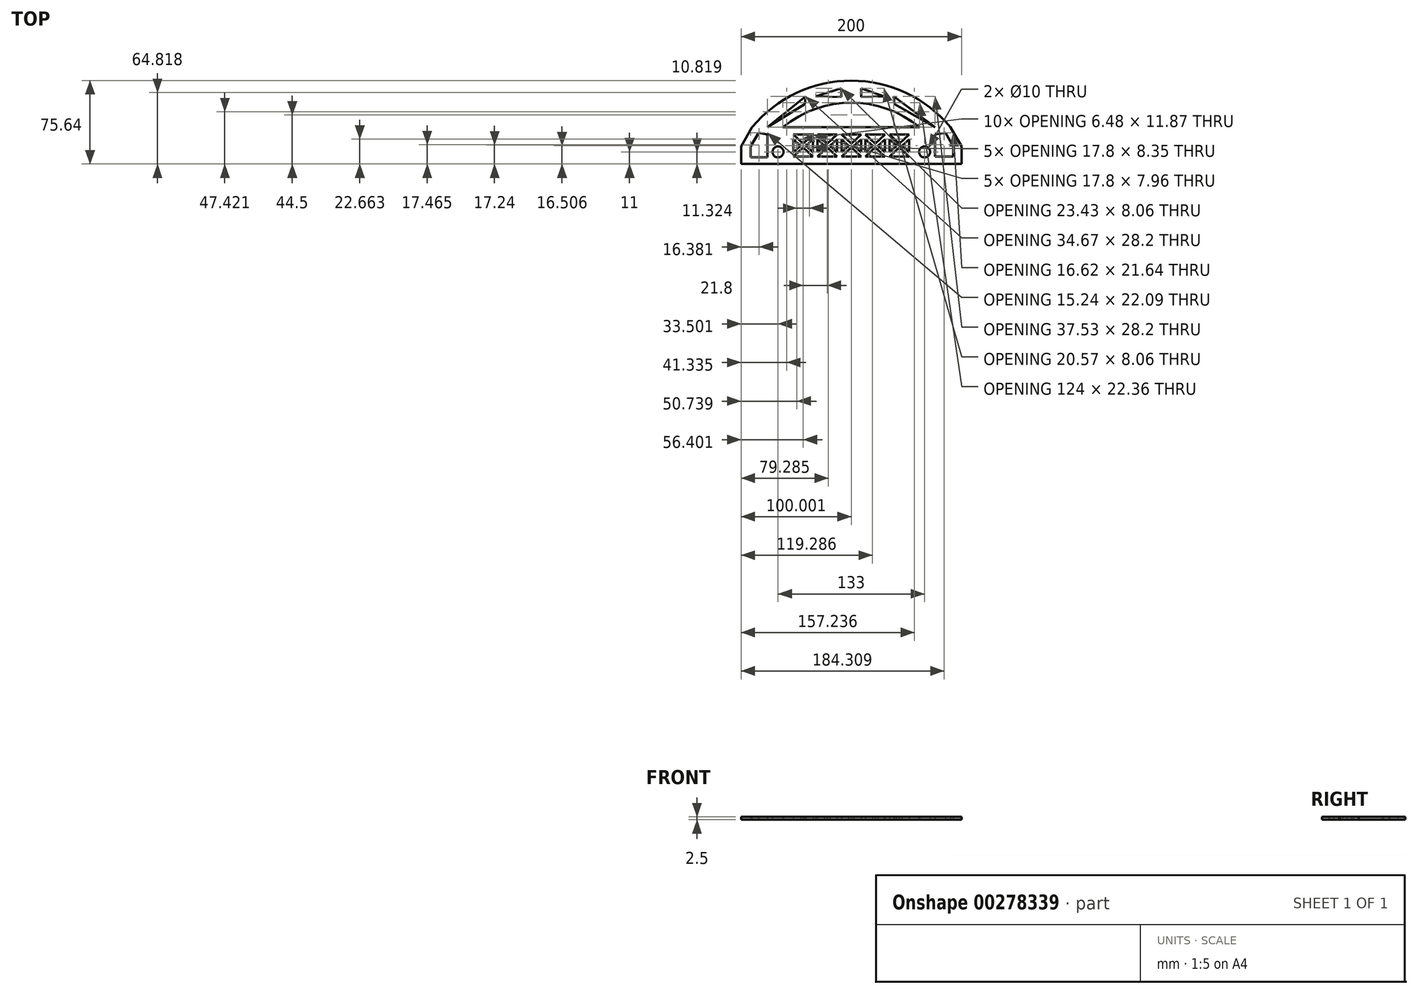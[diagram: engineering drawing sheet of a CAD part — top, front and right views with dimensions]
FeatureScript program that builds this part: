
annotation { "Feature Type Name" : "Feature", "Feature Type Description" : "" }
export const myFeature = defineFeature(function(context is Context, id is Id, definition is map)
    precondition{}
    {
        {
            var Q0;
            Q0=qCreatedBy(makeId("Top.planeOp"),FACE);
            var sketch = newSketch(context, id + "F0", { "sketchPlane" : qUnion([Q0])});
            skLineSegment(sketch, "E0.top", {"start": v(-97.14, -33.32) * mm, "end": v(102.86, -33.32) * mm});
            skLineSegment(sketch, "E0.left", {"start": v(-97.14, -17.32) * mm, "end": v(-97.14, -33.32) * mm});
            skLineSegment(sketch, "E0.right", {"start": v(102.86, -17.32) * mm, "end": v(102.86, -33.32) * mm});
            skCircle(sketch, "E1", {"center": v(-63.64, -22.32) * mm, "radius": 5 * mm});
            skCircle(sketch, "E2", {"center": v(69.36, -22.32) * mm, "radius": 5 * mm});
            skPoint(sketch, "E3", {"position": v(-63.64, -33.32) * mm});
            skPoint(sketch, "E4", {"position": v(69.36, -33.32) * mm});
            skLineSegment(sketch, "E5", {"start": v(-63.64, -33.32) * mm, "end": v(-97.14, -33.32) * mm});
            skLineSegment(sketch, "E6", {"start": v(69.36, -33.32) * mm, "end": v(102.86, -33.32) * mm});
            skLineSegment(sketch, "E7", {"start": v(-97.14, -17.32) * mm, "end": v(-87.14, 0) * mm});
            skLineSegment(sketch, "E8", {"start": v(102.86, -17.32) * mm, "end": v(92.86, 0) * mm});
            skArc(sketch, "E9", {"start": v(92.86, 0) * mm, "mid": v(2.86, 42.32) * mm, "end": v(-87.14, 0) * mm});
            skPoint(sketch, "E10", {"position": v(-59.14, 0) * mm});
            skPoint(sketch, "E11", {"position": v(64.86, 0) * mm});
            skArc(sketch, "E12", {"start": v(64.86, 0) * mm, "mid": v(2.86, 22.36) * mm, "end": v(-59.14, 0) * mm});
            skLineSegment(sketch, "E13", {"start": v(-59.14, 0) * mm, "end": v(64.86, 0) * mm});
            skLineSegment(sketch, "E14", {"start": v(0, 0) * mm, "end": v(-59.14, 0) * mm});
            skPoint(sketch, "E15", {"position": v(-29.57, 28.2) * mm});
            skPoint(sketch, "E15.positionSnap0", {"position": v(-29.57, 0) * mm});
            skLineSegment(sketch, "E16", {"start": v(0, 0) * mm, "end": v(64.86, 0) * mm});
            skPoint(sketch, "E17", {"position": v(32.43, 28.2) * mm});
            skPoint(sketch, "E17.positionSnap0", {"position": v(32.43, 0) * mm});
            skPoint(sketch, "E18", {"position": v(2.86, -33.32) * mm});
            skPoint(sketch, "E19", {"position": v(2.86, 32.96) * mm});
            skLineSegment(sketch, "E20", {"start": v(11.86, 35.53) * mm, "end": v(11.86, 27.47) * mm});
            skLineSegment(sketch, "E21", {"start": v(-6.14, 35.53) * mm, "end": v(-6.14, 27.47) * mm});
            skLineSegment(sketch, "E22", {"start": v(11.86, 35.53) * mm, "end": v(32.43, 28.2) * mm});
            skLineSegment(sketch, "E23", {"start": v(11.86, 27.47) * mm, "end": v(32.43, 28.2) * mm});
            skLineSegment(sketch, "E24", {"start": v(-6.14, 35.53) * mm, "end": v(-29.57, 28.2) * mm});
            skLineSegment(sketch, "E25", {"start": v(-6.14, 27.47) * mm, "end": v(-29.57, 28.2) * mm});
            skPoint(sketch, "E26", {"position": v(-73.14, 0) * mm});
            skLineSegment(sketch, "E27", {"start": v(-39.14, 21.24) * mm, "end": v(-73.14, 0) * mm});
            skPoint(sketch, "E28", {"position": v(78.86, 0) * mm});
            skPoint(sketch, "E29", {"position": v(42, 21.24) * mm});
            skLineSegment(sketch, "E30", {"start": v(42, 21.24) * mm, "end": v(78.86, 0) * mm});
            skPoint(sketch, "E31", {"position": v(-38.47, 28.2) * mm});
            skLineSegment(sketch, "E32", {"start": v(-38.47, 28.2) * mm, "end": v(-73.14, 0) * mm});
            skLineSegment(sketch, "E33", {"start": v(-38.47, 28.2) * mm, "end": v(-39.14, 21.24) * mm});
            skPoint(sketch, "E34", {"position": v(41.33, 28.2) * mm});
            skLineSegment(sketch, "E35", {"start": v(41.33, 28.2) * mm, "end": v(42, 21.24) * mm});
            skLineSegment(sketch, "E36", {"start": v(41.33, 28.2) * mm, "end": v(78.86, 0) * mm});
            skPoint(sketch, "E37", {"position": v(-49.64, -6.67) * mm});
            skPoint(sketch, "E38", {"position": v(-31.84, -6.67) * mm});
            skLineSegment(sketch, "E39", {"start": v(-49.64, -6.67) * mm, "end": v(-31.84, -6.67) * mm});
            skPoint(sketch, "E40", {"position": v(-40.74, -14.64) * mm});
            skPoint(sketch, "E40.positionSnap0", {"position": v(-40.74, -6.67) * mm});
            skPoint(sketch, "E41", {"position": v(-40.74, -18.33) * mm});
            skPoint(sketch, "E42", {"position": v(-49.64, -26.67) * mm});
            skPoint(sketch, "E43", {"position": v(-31.84, -26.67) * mm});
            skLineSegment(sketch, "E44", {"start": v(-49.64, -26.67) * mm, "end": v(-40.74, -18.33) * mm});
            skLineSegment(sketch, "E45", {"start": v(-31.84, -26.67) * mm, "end": v(-40.74, -18.33) * mm});
            skLineSegment(sketch, "E46", {"start": v(-49.64, -26.67) * mm, "end": v(-31.84, -26.67) * mm});
            skLineSegment(sketch, "E47", {"start": v(-31.84, -6.67) * mm, "end": v(-40.74, -14.64) * mm});
            skLineSegment(sketch, "E48", {"start": v(-49.64, -6.67) * mm, "end": v(-40.74, -14.64) * mm});
            skPoint(sketch, "E49", {"position": v(-42.17, -16.67) * mm});
            skPoint(sketch, "E50", {"position": v(-49.64, -16.67) * mm});
            skPoint(sketch, "E51", {"position": v(-31.84, -16.67) * mm});
            skLineSegment(sketch, "E52", {"start": v(-40.74, -14.64) * mm, "end": v(-42.17, -16.67) * mm});
            skPoint(sketch, "E53", {"position": v(-43.16, -16.67) * mm});
            skPoint(sketch, "E54", {"position": v(-38.32, -16.67) * mm});
            skLineSegment(sketch, "E55", {"start": v(-43.16, -16.67) * mm, "end": v(-49.64, -10.88) * mm});
            skLineSegment(sketch, "E56", {"start": v(-43.16, -16.67) * mm, "end": v(-49.64, -22.75) * mm});
            skLineSegment(sketch, "E57", {"start": v(-49.64, -22.75) * mm, "end": v(-49.64, -10.88) * mm});
            skLineSegment(sketch, "E58", {"start": v(-38.32, -16.67) * mm, "end": v(-31.84, -10.88) * mm});
            skLineSegment(sketch, "E59", {"start": v(-38.32, -16.67) * mm, "end": v(-31.84, -22.75) * mm});
            skLineSegment(sketch, "E60", {"start": v(-31.84, -22.75) * mm, "end": v(-31.84, -10.88) * mm});
            skPoint(sketch, "E61.1.0.0", {"position": v(-21.36, -16.67) * mm});
            skPoint(sketch, "E61.1.0.1", {"position": v(-20.37, -16.67) * mm});
            skLineSegment(sketch, "E61.1.0.2", {"start": v(-21.36, -16.67) * mm, "end": v(-27.84, -10.88) * mm});
            skPoint(sketch, "E61.1.0.3", {"position": v(-16.52, -16.67) * mm});
            skPoint(sketch, "E61.1.0.4", {"position": v(-10.04, -16.67) * mm});
            skLineSegment(sketch, "E61.1.0.5", {"start": v(-21.36, -16.67) * mm, "end": v(-27.84, -22.75) * mm});
            skLineSegment(sketch, "E61.1.0.6", {"start": v(-27.84, -26.67) * mm, "end": v(-10.04, -26.67) * mm});
            skLineSegment(sketch, "E61.1.0.7", {"start": v(-10.04, -6.67) * mm, "end": v(-18.94, -14.64) * mm});
            skLineSegment(sketch, "E61.1.0.8", {"start": v(-27.84, -22.75) * mm, "end": v(-27.84, -10.88) * mm});
            skPoint(sketch, "E61.1.0.9", {"position": v(-27.84, -26.67) * mm});
            skPoint(sketch, "E61.1.0.10", {"position": v(-27.84, -6.67) * mm});
            skLineSegment(sketch, "E61.1.0.11", {"start": v(-10.04, -26.67) * mm, "end": v(-18.94, -18.33) * mm});
            skLineSegment(sketch, "E61.1.0.12", {"start": v(-16.52, -16.67) * mm, "end": v(-10.04, -10.88) * mm});
            skLineSegment(sketch, "E61.1.0.13", {"start": v(-27.84, -6.67) * mm, "end": v(-18.94, -14.64) * mm});
            skPoint(sketch, "E61.1.0.14", {"position": v(-27.84, -16.67) * mm});
            skPoint(sketch, "E61.1.0.15", {"position": v(-18.94, -18.33) * mm});
            skLineSegment(sketch, "E61.1.0.16", {"start": v(-27.84, -6.67) * mm, "end": v(-10.04, -6.67) * mm});
            skPoint(sketch, "E61.1.0.17", {"position": v(-10.04, -6.67) * mm});
            skPoint(sketch, "E61.1.0.18", {"position": v(-18.94, -6.67) * mm});
            skLineSegment(sketch, "E61.1.0.19", {"start": v(-10.04, -22.75) * mm, "end": v(-10.04, -10.88) * mm});
            skLineSegment(sketch, "E61.1.0.20", {"start": v(-27.84, -26.67) * mm, "end": v(-18.94, -18.33) * mm});
            skPoint(sketch, "E61.1.0.21", {"position": v(-18.94, -14.64) * mm});
            skLineSegment(sketch, "E61.1.0.22", {"start": v(-16.52, -16.67) * mm, "end": v(-10.04, -22.75) * mm});
            skPoint(sketch, "E61.1.0.23", {"position": v(-10.04, -26.67) * mm});
            skLineSegment(sketch, "E61.1.0.24", {"start": v(-18.94, -14.64) * mm, "end": v(-20.37, -16.67) * mm});
            skPoint(sketch, "E61.2.0.0", {"position": v(0.44, -16.67) * mm});
            skPoint(sketch, "E61.2.0.1", {"position": v(1.43, -16.67) * mm});
            skLineSegment(sketch, "E61.2.0.2", {"start": v(0.44, -16.67) * mm, "end": v(-6.04, -10.88) * mm});
            skPoint(sketch, "E61.2.0.3", {"position": v(5.28, -16.67) * mm});
            skPoint(sketch, "E61.2.0.4", {"position": v(11.76, -16.67) * mm});
            skLineSegment(sketch, "E61.2.0.5", {"start": v(0.44, -16.67) * mm, "end": v(-6.04, -22.75) * mm});
            skLineSegment(sketch, "E61.2.0.6", {"start": v(-6.04, -26.67) * mm, "end": v(11.76, -26.67) * mm});
            skLineSegment(sketch, "E61.2.0.7", {"start": v(11.76, -6.67) * mm, "end": v(2.86, -14.64) * mm});
            skLineSegment(sketch, "E61.2.0.8", {"start": v(-6.04, -22.75) * mm, "end": v(-6.04, -10.88) * mm});
            skPoint(sketch, "E61.2.0.9", {"position": v(-6.04, -26.67) * mm});
            skPoint(sketch, "E61.2.0.10", {"position": v(-6.04, -6.67) * mm});
            skLineSegment(sketch, "E61.2.0.11", {"start": v(11.76, -26.67) * mm, "end": v(2.86, -18.33) * mm});
            skLineSegment(sketch, "E61.2.0.12", {"start": v(5.28, -16.67) * mm, "end": v(11.76, -10.88) * mm});
            skLineSegment(sketch, "E61.2.0.13", {"start": v(-6.04, -6.67) * mm, "end": v(2.86, -14.64) * mm});
            skPoint(sketch, "E61.2.0.14", {"position": v(-6.04, -16.67) * mm});
            skPoint(sketch, "E61.2.0.15", {"position": v(2.86, -18.33) * mm});
            skLineSegment(sketch, "E61.2.0.16", {"start": v(-6.04, -6.67) * mm, "end": v(11.76, -6.67) * mm});
            skPoint(sketch, "E61.2.0.17", {"position": v(11.76, -6.67) * mm});
            skPoint(sketch, "E61.2.0.18", {"position": v(2.86, -6.67) * mm});
            skLineSegment(sketch, "E61.2.0.19", {"start": v(11.76, -22.75) * mm, "end": v(11.76, -10.88) * mm});
            skLineSegment(sketch, "E61.2.0.20", {"start": v(-6.04, -26.67) * mm, "end": v(2.86, -18.33) * mm});
            skPoint(sketch, "E61.2.0.21", {"position": v(2.86, -14.64) * mm});
            skLineSegment(sketch, "E61.2.0.22", {"start": v(5.28, -16.67) * mm, "end": v(11.76, -22.75) * mm});
            skPoint(sketch, "E61.2.0.23", {"position": v(11.76, -26.67) * mm});
            skLineSegment(sketch, "E61.2.0.24", {"start": v(2.86, -14.64) * mm, "end": v(1.43, -16.67) * mm});
            skPoint(sketch, "E61.3.0.0", {"position": v(22.24, -16.67) * mm});
            skPoint(sketch, "E61.3.0.1", {"position": v(23.23, -16.67) * mm});
            skLineSegment(sketch, "E61.3.0.2", {"start": v(22.24, -16.67) * mm, "end": v(15.76, -10.88) * mm});
            skPoint(sketch, "E61.3.0.3", {"position": v(27.08, -16.67) * mm});
            skPoint(sketch, "E61.3.0.4", {"position": v(33.56, -16.67) * mm});
            skLineSegment(sketch, "E61.3.0.5", {"start": v(22.24, -16.67) * mm, "end": v(15.76, -22.75) * mm});
            skLineSegment(sketch, "E61.3.0.6", {"start": v(15.76, -26.67) * mm, "end": v(33.56, -26.67) * mm});
            skLineSegment(sketch, "E61.3.0.7", {"start": v(33.56, -6.67) * mm, "end": v(24.66, -14.64) * mm});
            skLineSegment(sketch, "E61.3.0.8", {"start": v(15.76, -22.75) * mm, "end": v(15.76, -10.88) * mm});
            skPoint(sketch, "E61.3.0.9", {"position": v(15.76, -26.67) * mm});
            skPoint(sketch, "E61.3.0.10", {"position": v(15.76, -6.67) * mm});
            skLineSegment(sketch, "E61.3.0.11", {"start": v(33.56, -26.67) * mm, "end": v(24.66, -18.33) * mm});
            skLineSegment(sketch, "E61.3.0.12", {"start": v(27.08, -16.67) * mm, "end": v(33.56, -10.88) * mm});
            skLineSegment(sketch, "E61.3.0.13", {"start": v(15.76, -6.67) * mm, "end": v(24.66, -14.64) * mm});
            skPoint(sketch, "E61.3.0.14", {"position": v(15.76, -16.67) * mm});
            skPoint(sketch, "E61.3.0.15", {"position": v(24.66, -18.33) * mm});
            skLineSegment(sketch, "E61.3.0.16", {"start": v(15.76, -6.67) * mm, "end": v(33.56, -6.67) * mm});
            skPoint(sketch, "E61.3.0.17", {"position": v(33.56, -6.67) * mm});
            skPoint(sketch, "E61.3.0.18", {"position": v(24.66, -6.67) * mm});
            skLineSegment(sketch, "E61.3.0.19", {"start": v(33.56, -22.75) * mm, "end": v(33.56, -10.88) * mm});
            skLineSegment(sketch, "E61.3.0.20", {"start": v(15.76, -26.67) * mm, "end": v(24.66, -18.33) * mm});
            skPoint(sketch, "E61.3.0.21", {"position": v(24.66, -14.64) * mm});
            skLineSegment(sketch, "E61.3.0.22", {"start": v(27.08, -16.67) * mm, "end": v(33.56, -22.75) * mm});
            skPoint(sketch, "E61.3.0.23", {"position": v(33.56, -26.67) * mm});
            skLineSegment(sketch, "E61.3.0.24", {"start": v(24.66, -14.64) * mm, "end": v(23.23, -16.67) * mm});
            skPoint(sketch, "E61.4.0.0", {"position": v(44.04, -16.67) * mm});
            skPoint(sketch, "E61.4.0.1", {"position": v(45.03, -16.67) * mm});
            skLineSegment(sketch, "E61.4.0.2", {"start": v(44.04, -16.67) * mm, "end": v(37.56, -10.88) * mm});
            skPoint(sketch, "E61.4.0.3", {"position": v(48.88, -16.67) * mm});
            skPoint(sketch, "E61.4.0.4", {"position": v(55.36, -16.67) * mm});
            skLineSegment(sketch, "E61.4.0.5", {"start": v(44.04, -16.67) * mm, "end": v(37.56, -22.75) * mm});
            skLineSegment(sketch, "E61.4.0.6", {"start": v(37.56, -26.67) * mm, "end": v(55.36, -26.67) * mm});
            skLineSegment(sketch, "E61.4.0.7", {"start": v(55.36, -6.67) * mm, "end": v(46.46, -14.64) * mm});
            skLineSegment(sketch, "E61.4.0.8", {"start": v(37.56, -22.75) * mm, "end": v(37.56, -10.88) * mm});
            skPoint(sketch, "E61.4.0.9", {"position": v(37.56, -26.67) * mm});
            skPoint(sketch, "E61.4.0.10", {"position": v(37.56, -6.67) * mm});
            skLineSegment(sketch, "E61.4.0.11", {"start": v(55.36, -26.67) * mm, "end": v(46.46, -18.33) * mm});
            skLineSegment(sketch, "E61.4.0.12", {"start": v(48.88, -16.67) * mm, "end": v(55.36, -10.88) * mm});
            skLineSegment(sketch, "E61.4.0.13", {"start": v(37.56, -6.67) * mm, "end": v(46.46, -14.64) * mm});
            skPoint(sketch, "E61.4.0.14", {"position": v(37.56, -16.67) * mm});
            skPoint(sketch, "E61.4.0.15", {"position": v(46.46, -18.33) * mm});
            skLineSegment(sketch, "E61.4.0.16", {"start": v(37.56, -6.67) * mm, "end": v(55.36, -6.67) * mm});
            skPoint(sketch, "E61.4.0.17", {"position": v(55.36, -6.67) * mm});
            skPoint(sketch, "E61.4.0.18", {"position": v(46.46, -6.67) * mm});
            skLineSegment(sketch, "E61.4.0.19", {"start": v(55.36, -22.75) * mm, "end": v(55.36, -10.88) * mm});
            skLineSegment(sketch, "E61.4.0.20", {"start": v(37.56, -26.67) * mm, "end": v(46.46, -18.33) * mm});
            skPoint(sketch, "E61.4.0.21", {"position": v(46.46, -14.64) * mm});
            skLineSegment(sketch, "E61.4.0.22", {"start": v(48.88, -16.67) * mm, "end": v(55.36, -22.75) * mm});
            skPoint(sketch, "E61.4.0.23", {"position": v(55.36, -26.67) * mm});
            skLineSegment(sketch, "E61.4.0.24", {"start": v(46.46, -14.64) * mm, "end": v(45.03, -16.67) * mm});
            skLineSegment(sketch, "E61.direction1", {"start": v(-49.64, -26.67) * mm, "end": v(-27.84, -26.67) * mm, "construction": true});
            skLineSegment(sketch, "E62", {"start": v(-81.29, -5.04) * mm, "end": v(-88.38, -17.32) * mm});
            skLineSegment(sketch, "E63", {"start": v(-88.38, -17.32) * mm, "end": v(-88.38, -27.12) * mm});
            skLineSegment(sketch, "E64", {"start": v(-88.38, -27.12) * mm, "end": v(-73.14, -27.12) * mm});
            skLineSegment(sketch, "E65", {"start": v(-73.14, -27.12) * mm, "end": v(-73.14, -6.67) * mm});
            skLineSegment(sketch, "E66", {"start": v(-73.14, -6.67) * mm, "end": v(-81.29, -5.04) * mm});
            skPoint(sketch, "E67", {"position": v(88.38, -5.04) * mm});
            skPoint(sketch, "E68", {"position": v(78.86, -6.67) * mm});
            skPoint(sketch, "E69", {"position": v(95.48, -17.32) * mm});
            skLineSegment(sketch, "E70", {"start": v(95.48, -17.32) * mm, "end": v(88.38, -5.04) * mm});
            skPoint(sketch, "E71", {"position": v(78.86, -26.67) * mm});
            skPoint(sketch, "E72", {"position": v(95.48, -26.67) * mm});
            skLineSegment(sketch, "E73", {"start": v(88.38, -5.04) * mm, "end": v(78.86, -6.67) * mm});
            skLineSegment(sketch, "E74", {"start": v(78.86, -26.67) * mm, "end": v(95.48, -26.67) * mm});
            skLineSegment(sketch, "E75", {"start": v(95.48, -17.32) * mm, "end": v(95.48, -26.67) * mm});
            skLineSegment(sketch, "E76", {"start": v(78.86, -6.67) * mm, "end": v(78.86, -26.67) * mm});
            skSolve(sketch);
        }
        {
            var Q0;
            Q0=makeQuery(id+"F0.imprint","IMPRINT",FACE,{"disambiguationData":[TD([[makeQuery(id+"F0.imprint","IMPRINT",EDGE,{"derivedFrom":sQuery(id+"F0.wireOp",EDGE,"E0.top")}),1.0]])]});
            extrude(context, id + "F1", {"entities" : qUnion([Q0]), "depth" : 2.5 * mm});
        }
    });
